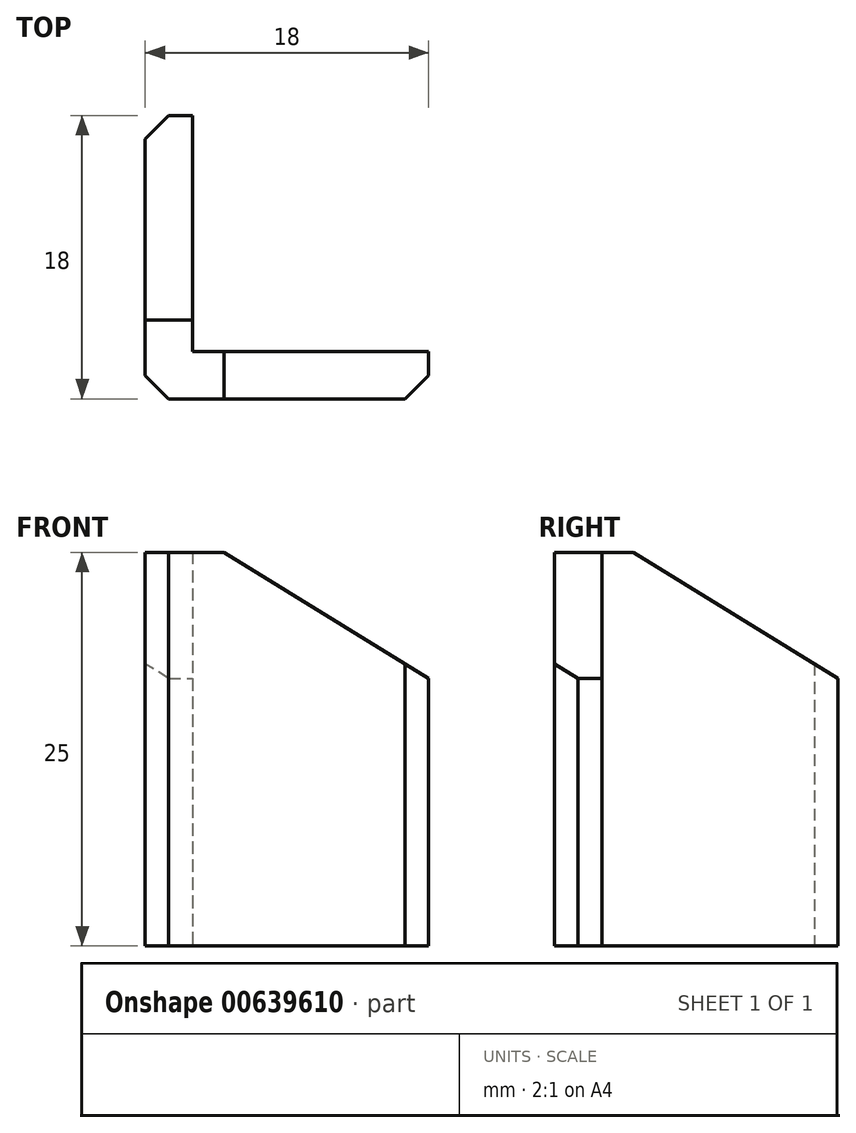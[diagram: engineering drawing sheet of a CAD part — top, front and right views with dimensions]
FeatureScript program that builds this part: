
annotation { "Feature Type Name" : "Feature", "Feature Type Description" : "" }
export const myFeature = defineFeature(function(context is Context, id is Id, definition is map)
    precondition{}
    {
        {
            var Q0;
            Q0=qCreatedBy(makeId("Top.planeOp"),FACE);
            var sketch = newSketch(context, id + "F0", { "sketchPlane" : qUnion([Q0])});
            skLineSegment(sketch, "E0", {"start": v(0, 0) * mm, "end": v(0, 18) * mm});
            skLineSegment(sketch, "E1", {"start": v(0, 18) * mm, "end": v(3, 18) * mm});
            skLineSegment(sketch, "E2", {"start": v(3, 18) * mm, "end": v(3, 3) * mm});
            skLineSegment(sketch, "E3", {"start": v(3, 3) * mm, "end": v(18, 3) * mm});
            skLineSegment(sketch, "E4", {"start": v(18, 3) * mm, "end": v(18, 0) * mm});
            skLineSegment(sketch, "E5", {"start": v(18, 0) * mm, "end": v(0, 0) * mm});
            skSolve(sketch);
        }
        {
            var Q0;
            Q0 = qSketchRegion(id + "F0", true);
            extrude(context, id + "F1", {"entities" : qUnion([Q0]), "depth" : 25 * mm, "offsetDistance" : 25 * mm});
        }
        {
            var Q0;
            Q0=makeQuery(id+"F1.opExtrude","CAP_EDGE",EDGE,{"disambiguationData":[OSD([sQuery(id+"F0.wireOp",EDGE,"E1")])],"isStart":false});
            var Q1;
            Q1=makeQuery(id+"F1.opExtrude","CAP_EDGE",EDGE,{"disambiguationData":[OSD([sQuery(id+"F0.wireOp",EDGE,"E4")])],"isStart":false});
            chamfer(context, id + "F2", {"entities" : qUnion([Q0, Q1]), "chamferType" : ChamferType.TWO_OFFSETS, "width1" : 8 * mm, "oppositeDirection" : false, "width2" : 13 * mm, "tangentPropagation" : true});
        }
        {
            var Q0;
            Q0=makeQuery(id+"F1.opExtrude","SWEPT_EDGE",EDGE,{"disambiguationData":[OSD([sQuery(id+"F0.wireOp",EDGE,"E0"),sQuery(id+"F0.wireOp",EDGE,"E1")])]});
            var Q1;
            Q1=makeQuery(id+"F1.opExtrude","SWEPT_EDGE",EDGE,{"disambiguationData":[OSD([sQuery(id+"F0.wireOp",EDGE,"E0"),sQuery(id+"F0.wireOp",EDGE,"E5")])]});
            var Q2;
            Q2=makeQuery(id+"F1.opExtrude","SWEPT_EDGE",EDGE,{"disambiguationData":[OSD([sQuery(id+"F0.wireOp",EDGE,"E4"),sQuery(id+"F0.wireOp",EDGE,"E5")])]});
            chamfer(context, id + "F3", {"entities" : qUnion([Q0, Q1, Q2]), "width" : 1.5 * mm, "tangentPropagation" : true});
        }
    });
